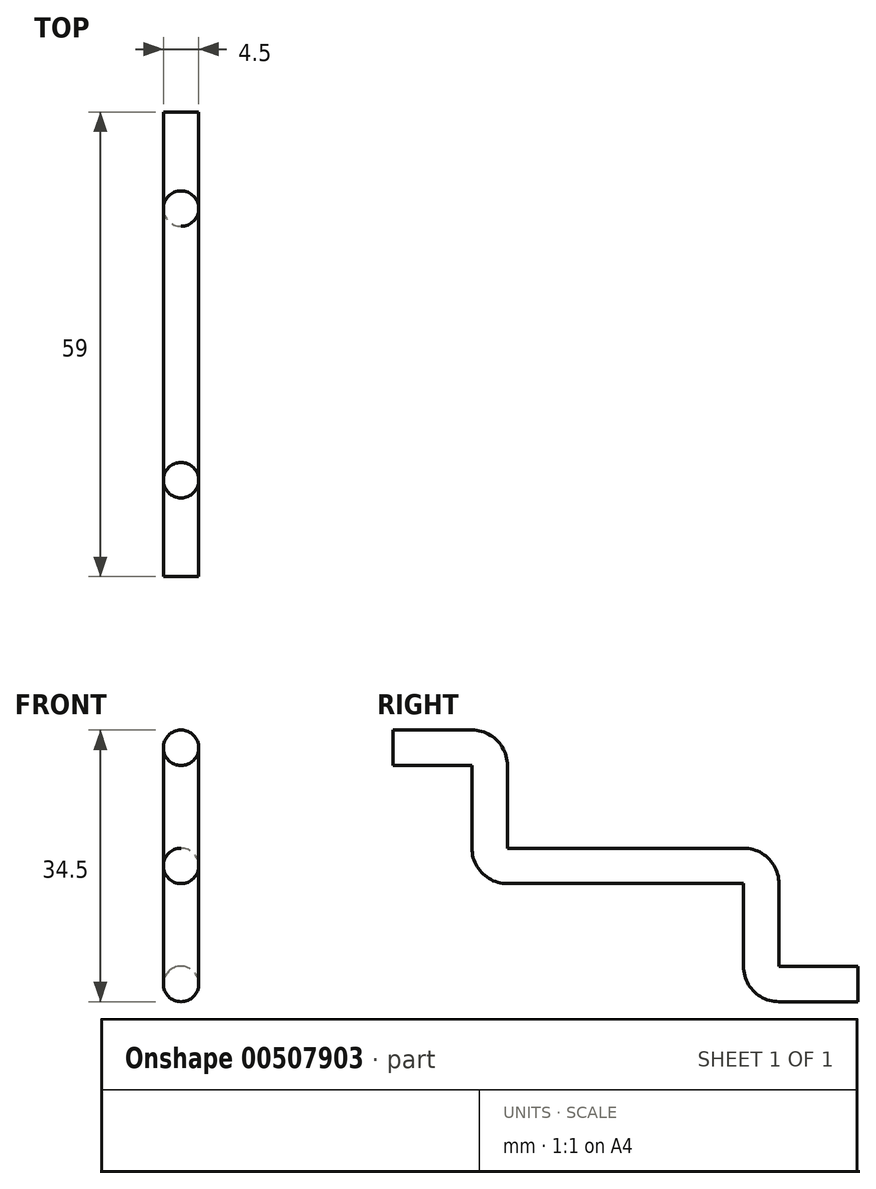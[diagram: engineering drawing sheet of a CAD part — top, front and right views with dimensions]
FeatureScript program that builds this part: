
annotation { "Feature Type Name" : "Feature", "Feature Type Description" : "" }
export const myFeature = defineFeature(function(context is Context, id is Id, definition is map)
    precondition{}
    {
        {
            var Q0;
            Q0=qCreatedBy(makeId("Front.planeOp"),FACE);
            var sketch = newSketch(context, id + "F0", { "sketchPlane" : qUnion([Q0])});
            skCircle(sketch, "E0", {"center": v(0, 0) * mm, "radius": 2.25 * mm});
            skLineSegment(sketch, "E1", {"start": v(-2.25, 25) * mm, "end": v(2.25, 25) * mm});
            skSolve(sketch);
        }
        {
            var Q0;
            Q0=makeQuery(id+"F0.imprint","IMPRINT",FACE,{"disambiguationData":[TD([[makeQuery(id+"F0.imprint","IMPRINT",EDGE,{"derivedFrom":sQuery(id+"F0.wireOp",EDGE,"E0")}),1.0]])]});
            extrude(context, id + "F1", {"entities" : qUnion([Q0]), "depth" : 30 * mm, "offsetDistance" : 25 * mm, "symmetric" : true});
        }
        {
            var Q0;
            Q0=qCreatedBy(makeId("Right.planeOp"),FACE);
            var sketch = newSketch(context, id + "F2", { "sketchPlane" : qUnion([Q0])});
            skLineSegment(sketch, "E2", {"start": v(0, 0) * mm, "end": v(-17.25, 0) * mm, "construction": true});
            skLineSegment(sketch, "E3", {"start": v(-17.25, 0) * mm, "end": v(-17.25, 2.25) * mm, "construction": true});
            skArc(sketch, "E4", {"start": v(-17.25, 2.25) * mm, "mid": v(-16.6, 0.66) * mm, "end": v(-15, 0) * mm});
            skLineSegment(sketch, "E5", {"start": v(0, 0) * mm, "end": v(17.25, 0) * mm, "construction": true});
            skLineSegment(sketch, "E6", {"start": v(17.25, 0) * mm, "end": v(17.25, -2.25) * mm, "construction": true});
            skArc(sketch, "E7", {"start": v(17.25, -2.25) * mm, "mid": v(16.6, -0.66) * mm, "end": v(15, 0) * mm});
            skSolve(sketch);
        }
        {
            var Q0;
            Q0=makeQuery(id+"F1.opExtrude","CAP_FACE",FACE,{"disambiguationData":[OSD([sQuery(id+"F0.wireOp",EDGE,"E0")])],"isStart":false});
            var Q1;
            Q1=sQuery(id+"F2.wireOp",EDGE,"E4");
            sweep(context, id + "F3", {"operationType" : NewBodyOperationType.ADD, "profiles" : qUnion([Q0]), "path" : qUnion([Q1])});
        }
        {
            var Q0;
            Q0=makeQuery(id+"F1.opExtrude","CAP_FACE",FACE,{"disambiguationData":[OSD([sQuery(id+"F0.wireOp",EDGE,"E0")])],"isStart":true});
            var Q1;
            Q1=sQuery(id+"F2.wireOp",EDGE,"E7");
            sweep(context, id + "F4", {"operationType" : NewBodyOperationType.ADD, "profiles" : qUnion([Q0]), "path" : qUnion([Q1])});
        }
        {
            var Q0;
            Q0=makeQuery(id+"F3.opSweep","CAP_FACE",FACE,{"disambiguationData":[OSD([sQuery(id+"F0.wireOp",EDGE,"E0"),sQuery(id+"F2.wireOp",VERTEX,"E4.start")])],"isStart":false});
            extrude(context, id + "F5", {"entities" : qUnion([Q0]), "operationType" : NewBodyOperationType.ADD, "depth" : 10.5 * mm, "offsetDistance" : 25 * mm});
        }
        {
            var Q0;
            Q0=makeQuery(id+"F4.opSweep","CAP_FACE",FACE,{"disambiguationData":[OSD([sQuery(id+"F0.wireOp",EDGE,"E0"),sQuery(id+"F2.wireOp",VERTEX,"E7.start")])],"isStart":false});
            extrude(context, id + "F6", {"entities" : qUnion([Q0]), "operationType" : NewBodyOperationType.ADD, "depth" : 10.5 * mm, "offsetDistance" : 25 * mm});
        }
        {
            var Q0;
            Q0=qCreatedBy(makeId("Right.planeOp"),FACE);
            var sketch = newSketch(context, id + "F7", { "sketchPlane" : qUnion([Q0])});
            skLineSegment(sketch, "E8", {"start": v(0, 0) * mm, "end": v(0, -15) * mm, "construction": true});
            skLineSegment(sketch, "E9", {"start": v(0, -15) * mm, "end": v(17.25, -15) * mm, "construction": true});
            skLineSegment(sketch, "E10", {"start": v(17.25, -15) * mm, "end": v(17.25, 0) * mm, "construction": true});
            skLineSegment(sketch, "E11", {"start": v(17.25, -15) * mm, "end": v(19.5, -15) * mm, "construction": true});
            skArc(sketch, "E12", {"start": v(17.25, -12.75) * mm, "mid": v(17.9, -14.34) * mm, "end": v(19.5, -15) * mm});
            skLineSegment(sketch, "E13", {"start": v(0, 0) * mm, "end": v(0, 15) * mm, "construction": true});
            skLineSegment(sketch, "E14", {"start": v(0, 15) * mm, "end": v(-17.25, 15) * mm, "construction": true});
            skLineSegment(sketch, "E15", {"start": v(-17.25, 15) * mm, "end": v(-17.25, 0) * mm, "construction": true});
            skLineSegment(sketch, "E16", {"start": v(-17.25, 15) * mm, "end": v(-19.5, 15) * mm, "construction": true});
            skArc(sketch, "E17", {"start": v(-17.25, 12.75) * mm, "mid": v(-17.9, 14.34) * mm, "end": v(-19.5, 15) * mm});
            skSolve(sketch);
        }
        {
            var Q0;
            Q0=makeQuery(id+"F6.opExtrude","CAP_FACE",FACE,{"disambiguationData":[OSD([sQuery(id+"F0.wireOp",EDGE,"E0"),sQuery(id+"F2.wireOp",VERTEX,"E7.start")])],"isStart":false});
            var Q1;
            Q1=sQuery(id+"F7.wireOp",EDGE,"E12");
            sweep(context, id + "F8", {"operationType" : NewBodyOperationType.ADD, "profiles" : qUnion([Q0]), "path" : qUnion([Q1])});
        }
        {
            var Q0;
            Q0=makeQuery(id+"F5.opExtrude","CAP_FACE",FACE,{"disambiguationData":[OSD([sQuery(id+"F0.wireOp",EDGE,"E0"),sQuery(id+"F2.wireOp",VERTEX,"E4.start")])],"isStart":false});
            var Q1;
            Q1=sQuery(id+"F7.wireOp",EDGE,"E17");
            sweep(context, id + "F9", {"operationType" : NewBodyOperationType.ADD, "profiles" : qUnion([Q0]), "path" : qUnion([Q1])});
        }
        {
            var Q0;
            Q0=makeQuery(id+"F9.opSweep","CAP_FACE",FACE,{"disambiguationData":[OSD([sQuery(id+"F0.wireOp",EDGE,"E0"),sQuery(id+"F2.wireOp",VERTEX,"E4.start"),sQuery(id+"F7.wireOp",VERTEX,"E17.end")])],"isStart":false});
            extrude(context, id + "F10", {"entities" : qUnion([Q0]), "operationType" : NewBodyOperationType.ADD, "depth" : 10 * mm, "offsetDistance" : 25 * mm});
        }
        {
            var Q0;
            Q0=makeQuery(id+"F8.opSweep","CAP_FACE",FACE,{"disambiguationData":[OSD([sQuery(id+"F0.wireOp",EDGE,"E0"),sQuery(id+"F2.wireOp",VERTEX,"E7.start"),sQuery(id+"F7.wireOp",VERTEX,"E12.end")])],"isStart":false});
            extrude(context, id + "F11", {"entities" : qUnion([Q0]), "operationType" : NewBodyOperationType.ADD, "depth" : 10 * mm, "offsetDistance" : 25 * mm});
        }
    });
